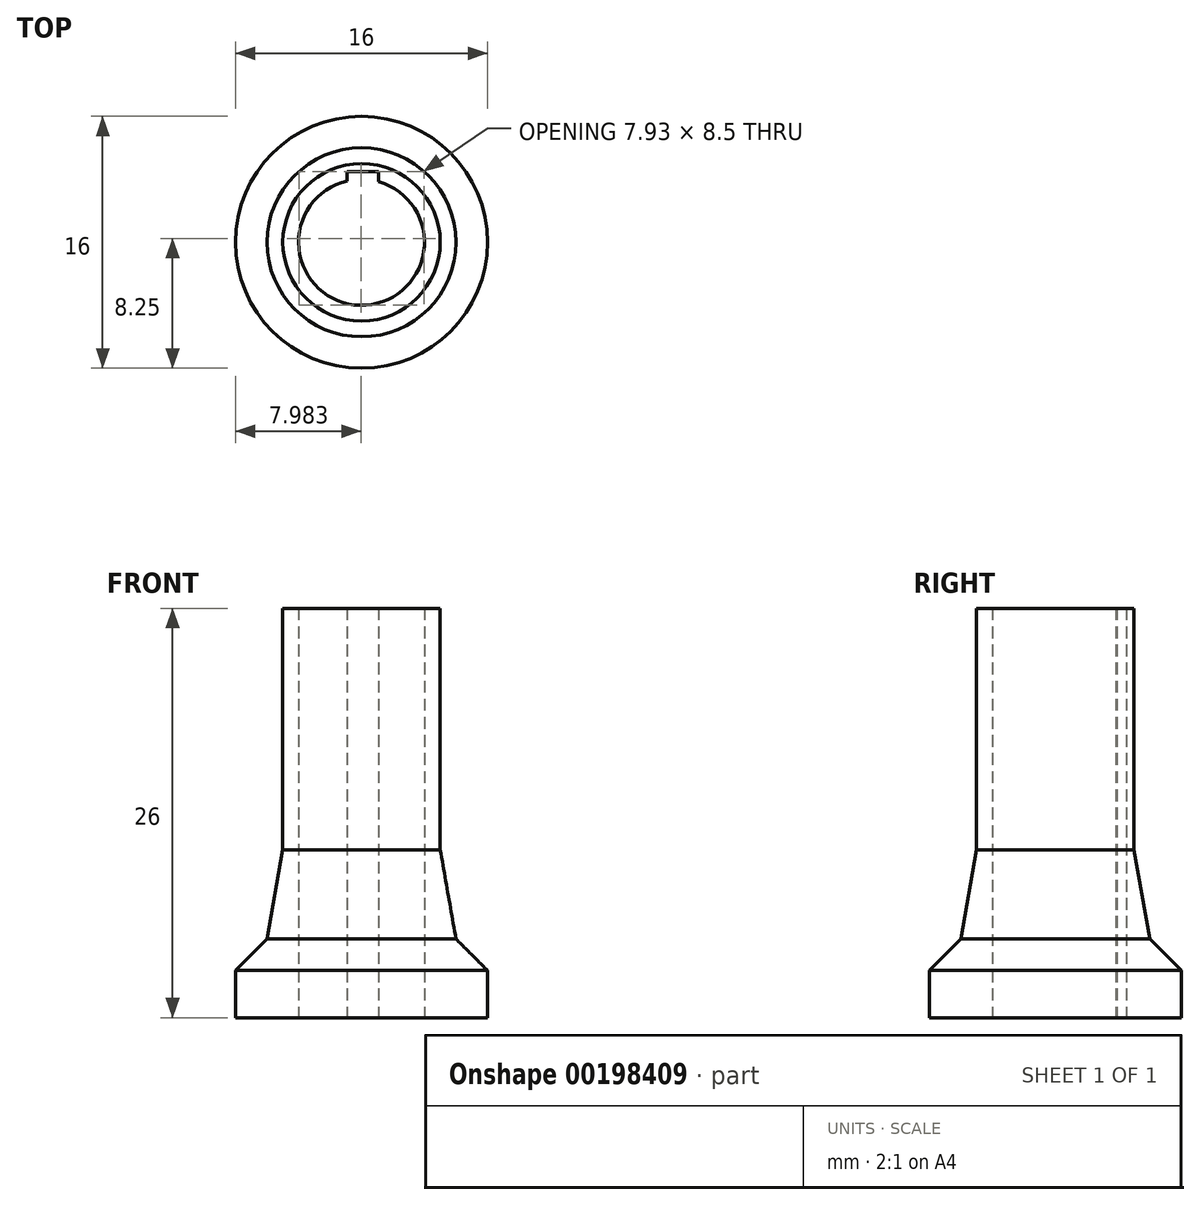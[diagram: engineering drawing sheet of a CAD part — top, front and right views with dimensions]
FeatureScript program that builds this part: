
annotation { "Feature Type Name" : "Feature", "Feature Type Description" : "" }
export const myFeature = defineFeature(function(context is Context, id is Id, definition is map)
    precondition{}
    {
        {
            var Q0;
            Q0=qCreatedBy(makeId("Front.planeOp"),FACE);
            var sketch = newSketch(context, id + "F0", { "sketchPlane" : qUnion([Q0])});
            skLineSegment(sketch, "E0", {"start": v(-3.45, -20.87) * mm, "end": v(-3.45, -17.87) * mm});
            skLineSegment(sketch, "E1", {"start": v(-3.45, -17.87) * mm, "end": v(-1.45, -15.87) * mm});
            skLineSegment(sketch, "E2", {"start": v(-1.45, -15.87) * mm, "end": v(-0.45, -10.2) * mm});
            skLineSegment(sketch, "E3", {"start": v(-3.45, -20.87) * mm, "end": v(-0.45, -20.87) * mm});
            skPoint(sketch, "E4.start.orphan", {"position": v(0.55, 53.13) * mm});
            skPoint(sketch, "E5.start.orphan", {"position": v(4.55, 53.13) * mm});
            skPoint(sketch, "E6.start.orphan", {"position": v(4.55, -29.87) * mm});
            skPoint(sketch, "E7.end.orphan", {"position": v(-0.45, -29.87) * mm});
            skLineSegment(sketch, "E8", {"start": v(-0.45, -20.87) * mm, "end": v(4.55, -20.87) * mm});
            skLineSegment(sketch, "E9", {"start": v(-0.45, -10.2) * mm, "end": v(-0.45, 5.13) * mm});
            skLineSegment(sketch, "E10", {"start": v(-0.45, 5.13) * mm, "end": v(4.55, 5.13) * mm});
            skLineSegment(sketch, "E11", {"start": v(4.55, 5.13) * mm, "end": v(4.55, -20.87) * mm});
            skSolve(sketch);
        }
        {
            var Q0;
            Q0=makeQuery(id+"F0.imprint","IMPRINT",FACE,{"disambiguationData":[TD([[makeQuery(id+"F0.imprint","IMPRINT",EDGE,{"derivedFrom":sQuery(id+"F0.wireOp",EDGE,"E0")}),-1.0]])]});
            var Q1;
            Q1=sQuery(id+"F0.wireOp",EDGE,"E11");
            revolve(context, id + "F1", {"entities" : qUnion([Q0]), "axis" : qUnion([Q1]), "revolveType" : RevolveType.FULL});
        }
        {
            var Q0;
            Q0=makeQuery(id+"F1.opRevolve","SWEPT_FACE",FACE,{"disambiguationData":[OSD([sQuery(id+"F0.wireOp",EDGE,"E3"),sQuery(id+"F0.wireOp",EDGE,"E8")])]});
            var sketch = newSketch(context, id + "F2", { "sketchPlane" : qUnion([Q0])});
            skArc(sketch, "E12", {"start": v(5.64, -3.85) * mm, "mid": v(4.45, 4) * mm, "end": v(3.64, -3.9) * mm});
            skPoint(sketch, "E13.middle", {"position": v(4.64, -4) * mm});
            skLineSegment(sketch, "E14.top", {"start": v(3.64, -4.5) * mm, "end": v(5.64, -4.5) * mm});
            skLineSegment(sketch, "E14.left", {"start": v(3.64, -3.9) * mm, "end": v(3.64, -4.5) * mm});
            skLineSegment(sketch, "E14.right", {"start": v(5.64, -3.85) * mm, "end": v(5.64, -4.5) * mm});
            skPoint(sketch, "E15.orphan", {"position": v(5.64, -3.5) * mm});
            skPoint(sketch, "E16.orphan", {"position": v(3.64, -3.5) * mm});
            skSolve(sketch);
        }
        {
            var Q0;
            Q0=makeQuery(id+"F2.imprint","IMPRINT",FACE,{"disambiguationData":[TD([[makeQuery(id+"F2.imprint","IMPRINT",EDGE,{"derivedFrom":sQuery(id+"F2.wireOp",EDGE,"E12")}),1.0]])]});
            extrude(context, id + "F3", {"entities" : qUnion([Q0]), "operationType" : NewBodyOperationType.REMOVE, "oppositeDirection" : true, "depth" : 30 * mm});
        }
    });
